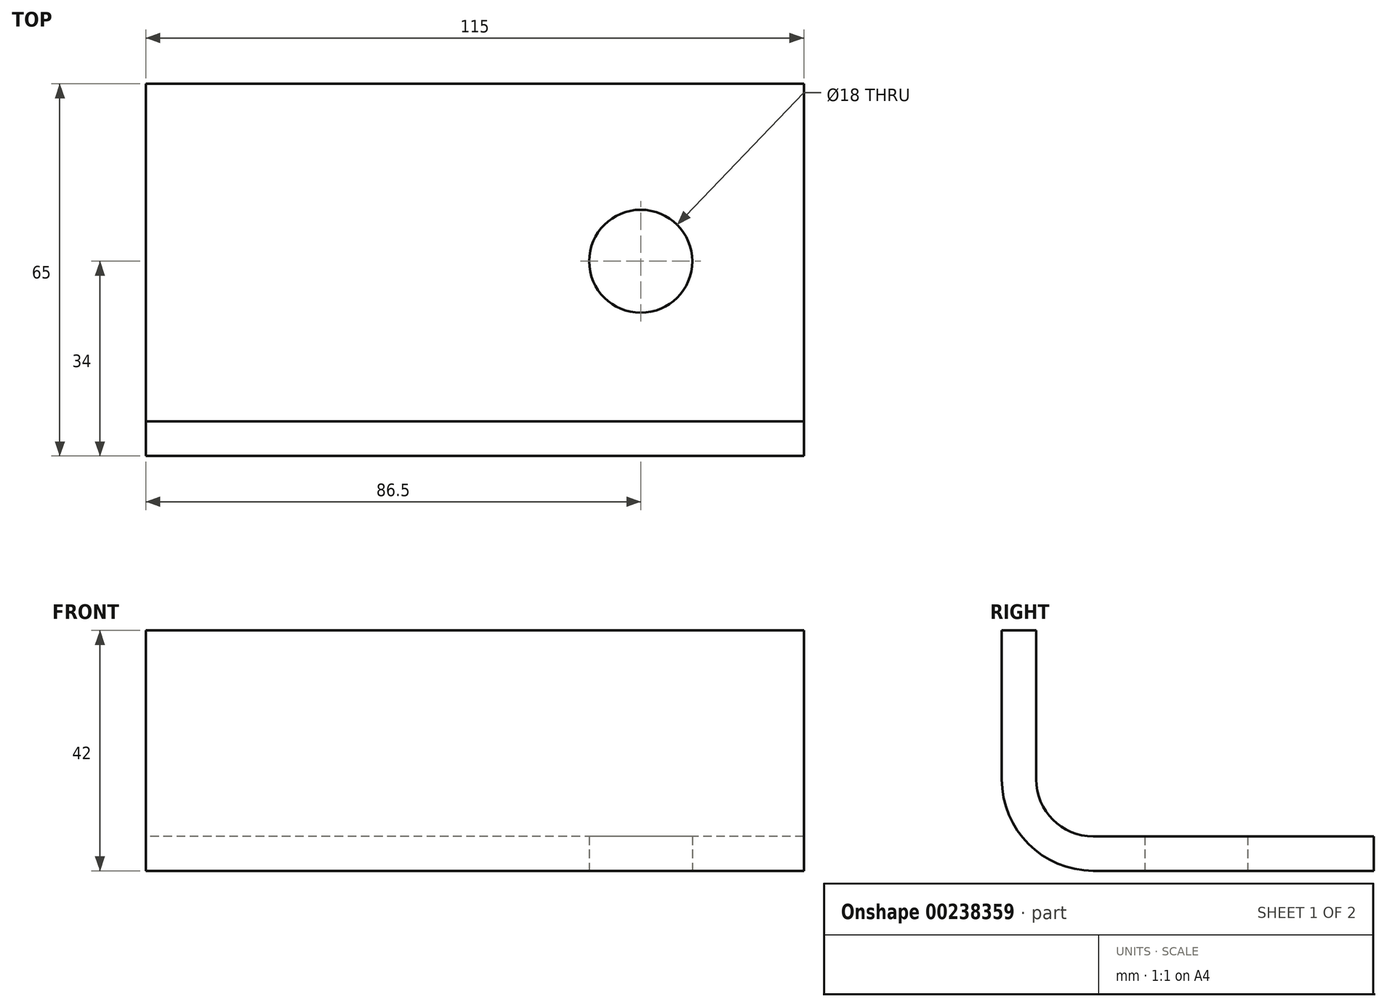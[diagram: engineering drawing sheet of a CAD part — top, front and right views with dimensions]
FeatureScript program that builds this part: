
annotation { "Feature Type Name" : "Feature", "Feature Type Description" : "" }
export const myFeature = defineFeature(function(context is Context, id is Id, definition is map)
    precondition{}
    {
        {
            var Q0;
            Q0=qCreatedBy(makeId("Right.planeOp"),FACE);
            var sketch = newSketch(context, id + "F0", { "sketchPlane" : qUnion([Q0])});
            skLineSegment(sketch, "E0", {"start": v(65, 0) * mm, "end": v(16, 0) * mm});
            skLineSegment(sketch, "E1", {"start": v(0, 16) * mm, "end": v(0, 42) * mm});
            skLineSegment(sketch, "E2", {"start": v(0, 42) * mm, "end": v(6, 42) * mm});
            skLineSegment(sketch, "E3", {"start": v(6, 42) * mm, "end": v(6, 16) * mm});
            skLineSegment(sketch, "E4", {"start": v(16, 6) * mm, "end": v(65, 6) * mm});
            skLineSegment(sketch, "E5", {"start": v(65, 6) * mm, "end": v(65, 0) * mm});
            skPoint(sketch, "E6.visualSharp", {"position": v(6, 6) * mm});
            skArc(sketch, "E6.filletArc", {"start": v(6, 16) * mm, "mid": v(8.93, 8.93) * mm, "end": v(16, 6) * mm});
            skPoint(sketch, "E7.visualSharp", {"position": v(0, 0) * mm});
            skArc(sketch, "E7.filletArc", {"start": v(0, 16) * mm, "mid": v(4.69, 4.69) * mm, "end": v(16, 0) * mm});
            skSolve(sketch);
        }
        {
            var Q0;
            Q0 = qSketchRegion(id + "F0", true);
            extrude(context, id + "F1", {"entities" : qUnion([Q0]), "depth" : 115 * mm});
        }
        {
            var Q0;
            Q0=makeQuery(id+"F1.opExtrude","SWEPT_FACE",FACE,{"disambiguationData":[OSD([sQuery(id+"F0.wireOp",EDGE,"E0")])]});
            var sketch = newSketch(context, id + "F2", { "sketchPlane" : qUnion([Q0])});
            skCircle(sketch, "E8", {"center": v(86.5, -34) * mm, "radius": 9 * mm});
            skSolve(sketch);
        }
        {
            var Q0;
            Q0 = qSketchRegion(id + "F2", true);
            extrude(context, id + "F3", {"entities" : qUnion([Q0]), "operationType" : NewBodyOperationType.REMOVE, "oppositeDirection" : true, "depth" : 25 * mm});
        }
    });
